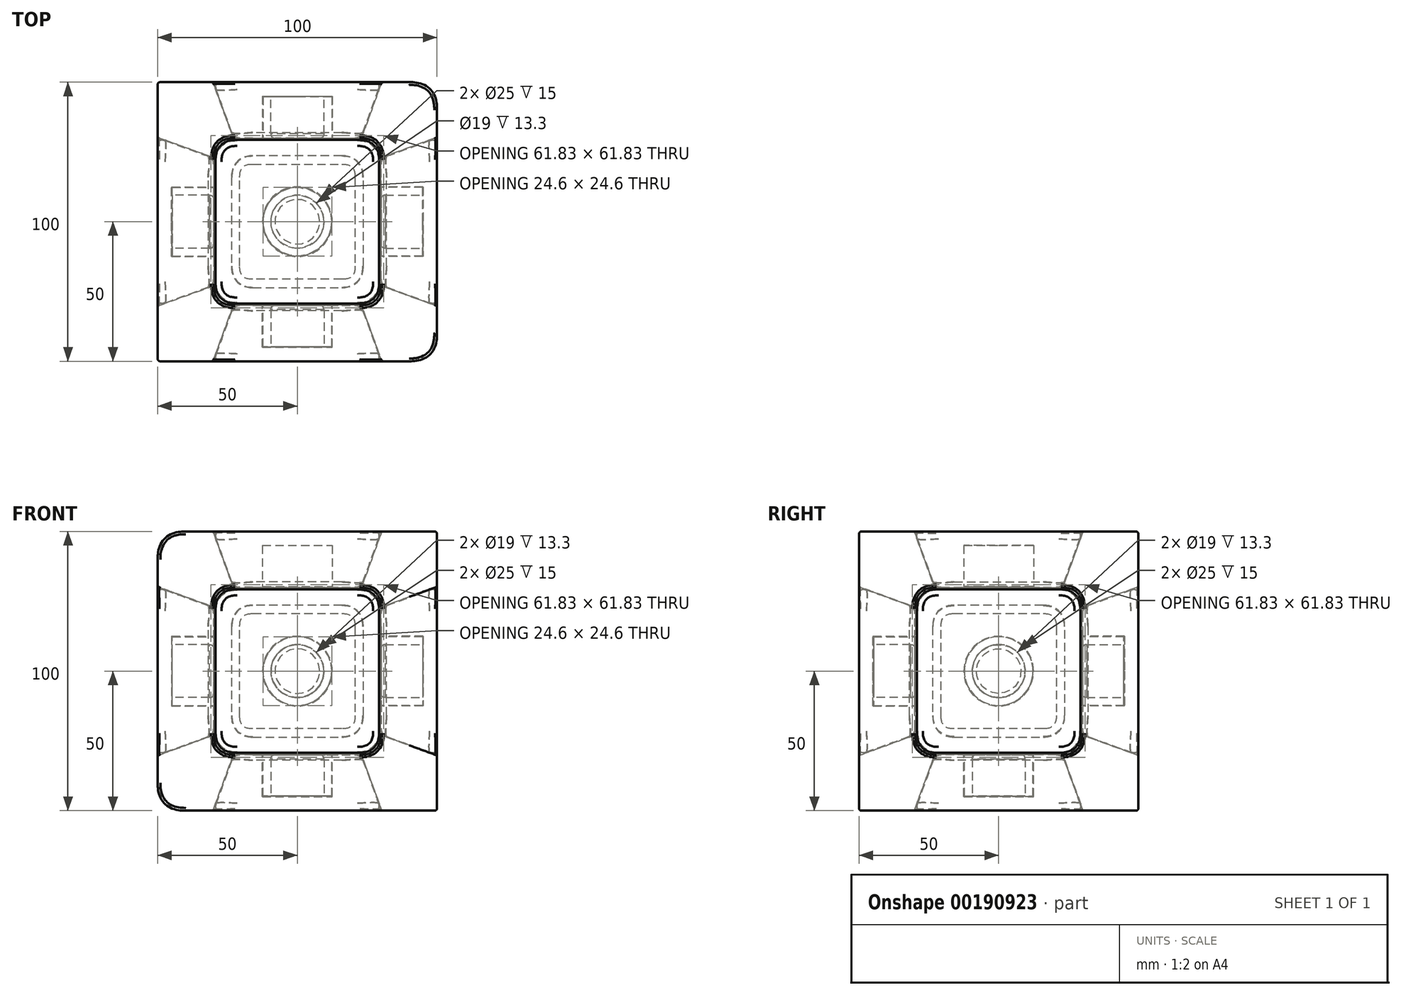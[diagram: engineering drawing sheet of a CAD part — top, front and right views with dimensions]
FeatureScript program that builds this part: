
annotation { "Feature Type Name" : "Feature", "Feature Type Description" : "" }
export const myFeature = defineFeature(function(context is Context, id is Id, definition is map)
    precondition{}
    {
        {
            var Q0;
            Q0=qCreatedBy(makeId("Top.planeOp"),FACE);
            var sketch = newSketch(context, id + "F0", { "sketchPlane" : qUnion([Q0])});
            skLineSegment(sketch, "E0.bottom", {"start": v(50, 50) * mm, "end": v(-50, 50) * mm});
            skLineSegment(sketch, "E0.top", {"start": v(50, -50) * mm, "end": v(-50, -50) * mm});
            skLineSegment(sketch, "E0.left", {"start": v(50, 50) * mm, "end": v(50, -50) * mm});
            skLineSegment(sketch, "E0.right", {"start": v(-50, 50) * mm, "end": v(-50, -50) * mm});
            skPoint(sketch, "E0.middle", {"position": v(0, 0) * mm});
            skSolve(sketch);
        }
        {
            var Q0;
            Q0=qSketchRegion(id+"F0",true);
            extrude(context, id + "F1", {"entities" : qUnion([Q0]), "depth" : 100 * mm, "offsetDistance" : 25 * mm, "symmetric" : true});
        }
        {
            var Q0;
            Q0=makeQuery(id+"F1.opExtrude","CAP_FACE",FACE,{"disambiguationData":[OSD([sQuery(id+"F0.wireOp",EDGE,"E0.bottom"),sQuery(id+"F0.wireOp",EDGE,"E0.top"),sQuery(id+"F0.wireOp",EDGE,"E0.left"),sQuery(id+"F0.wireOp",EDGE,"E0.right")])],"isStart":false});
            var sketch = newSketch(context, id + "F2", { "sketchPlane" : qUnion([Q0])});
            skLineSegment(sketch, "E1.0", {"start": v(30, 30) * mm, "end": v(-30, 30) * mm});
            skLineSegment(sketch, "E1.1", {"start": v(30, 30) * mm, "end": v(30, -30) * mm});
            skLineSegment(sketch, "E1.2", {"start": v(30, -30) * mm, "end": v(-30, -30) * mm});
            skLineSegment(sketch, "E1.3", {"start": v(-30, 30) * mm, "end": v(-30, -30) * mm});
            skSolve(sketch);
        }
        {
            var Q0;
            Q0=qSketchRegion(id+"F2",true);
            extrude(context, id + "F3", {"entities" : qUnion([Q0]), "oppositeDirection" : true, "depth" : 20 * mm, "offsetDistance" : 25 * mm, "hasDraft" : true, "draftAngle" : 20 * degree, "draftPullDirection" : true});
        }
        {
            var Q0;
            Q0=makeQuery(id+"F3.opExtrude","CAP_FACE",FACE,{"disambiguationData":[OSD([sQuery(id+"F2.wireOp",EDGE,"E1.0"),sQuery(id+"F2.wireOp",EDGE,"E1.1"),sQuery(id+"F2.wireOp",EDGE,"E1.2"),sQuery(id+"F2.wireOp",EDGE,"E1.3")])],"isStart":false});
            var sketch = newSketch(context, id + "F4", { "sketchPlane" : qUnion([Q0])});
            skCircle(sketch, "E2", {"center": v(0, 0) * mm, "radius": 12.5 * mm});
            skSolve(sketch);
        }
        {
            var Q0;
            Q0 = qSketchRegion(id + "F4", true);
            extrude(context, id + "F5", {"entities" : qUnion([Q0]), "operationType" : NewBodyOperationType.REMOVE, "oppositeDirection" : true, "depth" : 15 * mm, "offsetDistance" : 25 * mm});
        }
        {
            var Q0;
            Q0=makeQuery(id+"F5.boolean.opBoolean","COPY",FACE,{"derivedFrom":makeQuery(id+"F5.opExtrude","CAP_FACE",FACE,{"disambiguationData":[OSD([sQuery(id+"F4.wireOp",EDGE,"E2")])],"isStart":false})});
            var sketch = newSketch(context, id + "F6", { "sketchPlane" : qUnion([Q0])});
            skCircle(sketch, "E3.0", {"center": v(0, 0) * mm, "radius": 9.5 * mm});
            skSolve(sketch);
        }
        {
            var Q0;
            Q0=makeQuery(id+"F6.imprint","IMPRINT",FACE,{"disambiguationData":[TD([[makeQuery(id+"F6.imprint","IMPRINT",EDGE,{"derivedFrom":sQuery(id+"F6.wireOp",EDGE,"E3.0")}),1.0]])]});
            var Q1;
            Q1=makeQuery(id+"F3.opExtrude","CAP_FACE",FACE,{"disambiguationData":[OSD([sQuery(id+"F2.wireOp",EDGE,"E1.0"),sQuery(id+"F2.wireOp",EDGE,"E1.1"),sQuery(id+"F2.wireOp",EDGE,"E1.2"),sQuery(id+"F2.wireOp",EDGE,"E1.3")])],"isStart":false});
            extrude(context, id + "F7", {"entities" : qUnion([Q0]), "endBound" : BoundingType.UP_TO_SURFACE, "depth" : 25 * mm, "endBoundEntityFace" : qUnion([Q1]), "offsetDistance" : 25 * mm});
        }
        {
            var Q0;
            Q0=qCreatedBy(makeId("Top.planeOp"),FACE);
            var sketch = newSketch(context, id + "F8", { "sketchPlane" : qUnion([Q0])});
            skLineSegment(sketch, "E4", {"start": v(0, -64.23) * mm, "end": v(0, 63.51) * mm, "construction": true});
            skLineSegment(sketch, "E5", {"start": v(-60.37, 0) * mm, "end": v(65.94, 0) * mm, "construction": true});
            skSolve(sketch);
        }
        {
            var Q0;
            Q0=makeQuery(id+"F3.opExtrude","SWEPT_EDGE",EDGE,{"disambiguationData":[OSD([sQuery(id+"F2.wireOp",EDGE,"E1.1"),sQuery(id+"F2.wireOp",EDGE,"E1.2")])]});
            var Q1;
            Q1=makeQuery(id+"F3.opExtrude","SWEPT_EDGE",EDGE,{"disambiguationData":[OSD([sQuery(id+"F2.wireOp",EDGE,"E1.0"),sQuery(id+"F2.wireOp",EDGE,"E1.1")])]});
            var Q2;
            Q2=makeQuery(id+"F3.opExtrude","SWEPT_EDGE",EDGE,{"disambiguationData":[OSD([sQuery(id+"F2.wireOp",EDGE,"E1.2"),sQuery(id+"F2.wireOp",EDGE,"E1.3")])]});
            var Q3;
            Q3=makeQuery(id+"F3.opExtrude","SWEPT_EDGE",EDGE,{"disambiguationData":[OSD([sQuery(id+"F2.wireOp",EDGE,"E1.0"),sQuery(id+"F2.wireOp",EDGE,"E1.3")])]});
            fillet(context, id + "F9", {"entities" : qUnion([Q0, Q1, Q2, Q3]), "tangentPropagation" : true, "crossSection" : FilletCrossSection.CURVATURE, "radius" : 8 * mm, "magnitude" : 0.5, "defaultsChanged" : false, "vertexSettings" : []});
        }
        {
            var Q0;
            Q0=makeQuery(id+"F3.opExtrude","CAP_EDGE",EDGE,{"disambiguationData":[OSD([sQuery(id+"F2.wireOp",EDGE,"E1.1")])],"isStart":false});
            fillet(context, id + "F10", {"entities" : qUnion([Q0]), "tangentPropagation" : true, "crossSection" : FilletCrossSection.CURVATURE, "radius" : 3 * mm, "magnitude" : 0.5, "defaultsChanged" : false, "vertexSettings" : []});
        }
        {
            var Q0;
            Q0=makeQuery(id+"F5.boolean.opBoolean","COPY",EDGE,{"derivedFrom":makeQuery(id+"F5.opExtrude","CAP_EDGE",EDGE,{"disambiguationData":[OSD([sQuery(id+"F4.wireOp",EDGE,"E2")])],"isStart":true})});
            fillet(context, id + "F11", {"entities" : qUnion([Q0]), "tangentPropagation" : true, "crossSection" : FilletCrossSection.CURVATURE, "radius" : 1 * mm, "magnitude" : 0.5, "defaultsChanged" : false, "vertexSettings" : []});
        }
        {
            var Q0;
            Q0=makeQuery(id+"F7.opExtrude","CAP_FACE",FACE,{"disambiguationData":[OSD([sQuery(id+"F6.wireOp",EDGE,"E3.0")])],"isStart":false});
            fillet(context, id + "F12", {"entities" : qUnion([Q0]), "tangentPropagation" : true, "crossSection" : FilletCrossSection.CURVATURE, "radius" : 1.5 * mm, "magnitude" : 0.5, "defaultsChanged" : true, "vertexSettings" : []});
        }
        {
            var Q0;
            Q0=makeQuery(id+"F3.opExtrude","SWEPT_BODY",BODY,{"disambiguationData":[OSD([sQuery(id+"F2.wireOp",EDGE,"E1.0"),sQuery(id+"F2.wireOp",EDGE,"E1.1"),sQuery(id+"F2.wireOp",EDGE,"E1.2"),sQuery(id+"F2.wireOp",EDGE,"E1.3")])]});
            var Q1;
            Q1=makeQuery(id+"F7.opExtrude","SWEPT_BODY",BODY,{"disambiguationData":[OSD([sQuery(id+"F6.wireOp",EDGE,"E3.0")])]});
            var Q2;
            Q2=makeQuery(id+"F3.boolean.opBoolean","COPY",FACE,{"derivedFrom":makeQuery(id+"F3.opExtrude","CAP_FACE",FACE,{"disambiguationData":[OSD([sQuery(id+"F2.wireOp",EDGE,"E1.0"),sQuery(id+"F2.wireOp",EDGE,"E1.1"),sQuery(id+"F2.wireOp",EDGE,"E1.2"),sQuery(id+"F2.wireOp",EDGE,"E1.3")])],"isStart":false})});
            var Q3;
            Q3=makeQuery(id+"F3.boolean.opBoolean","COPY",FACE,{"derivedFrom":makeQuery(id+"F3.opExtrude","SWEPT_FACE",FACE,{"disambiguationData":[OSD([sQuery(id+"F2.wireOp",EDGE,"E1.3")])]})});
            var Q4;
            Q4=makeQuery(id+"F3.boolean.opBoolean","COPY",FACE,{"derivedFrom":makeQuery(id+"F3.opExtrude","SWEPT_FACE",FACE,{"disambiguationData":[OSD([sQuery(id+"F2.wireOp",EDGE,"E1.0")])]})});
            var Q5;
            Q5=makeQuery(id+"F3.boolean.opBoolean","COPY",FACE,{"derivedFrom":makeQuery(id+"F3.opExtrude","SWEPT_FACE",FACE,{"disambiguationData":[OSD([sQuery(id+"F2.wireOp",EDGE,"E1.1")])]})});
            var Q6;
            Q6=makeQuery(id+"F3.boolean.opBoolean","COPY",FACE,{"derivedFrom":makeQuery(id+"F3.opExtrude","SWEPT_FACE",FACE,{"disambiguationData":[OSD([sQuery(id+"F2.wireOp",EDGE,"E1.2")])]})});
            var Q7;
            Q7=sQuery(id+"F8.wireOp",EDGE,"E5");
            circularPattern(context, id + "F13", {"entities" : qUnion([Q0, Q1]), "axis" : qUnion([Q7]), "angle" : 360 * degree, "instanceCount" : 4, "equalSpace" : true});
        }
        {
            var Q0;
            Q0=makeQuery(id+"F3.opExtrude","SWEPT_BODY",BODY,{"disambiguationData":[OSD([sQuery(id+"F2.wireOp",EDGE,"E1.0"),sQuery(id+"F2.wireOp",EDGE,"E1.1"),sQuery(id+"F2.wireOp",EDGE,"E1.2"),sQuery(id+"F2.wireOp",EDGE,"E1.3")])]});
            var Q1;
            Q1=makeQuery(id+"F7.opExtrude","SWEPT_BODY",BODY,{"disambiguationData":[OSD([sQuery(id+"F6.wireOp",EDGE,"E3.0")])]});
            var Q2;
            Q2=makeQuery(id+"F3.boolean.opBoolean","COPY",FACE,{"derivedFrom":makeQuery(id+"F3.opExtrude","CAP_FACE",FACE,{"disambiguationData":[OSD([sQuery(id+"F2.wireOp",EDGE,"E1.0"),sQuery(id+"F2.wireOp",EDGE,"E1.1"),sQuery(id+"F2.wireOp",EDGE,"E1.2"),sQuery(id+"F2.wireOp",EDGE,"E1.3")])],"isStart":false})});
            var Q3;
            Q3=makeQuery(id+"F3.boolean.opBoolean","COPY",FACE,{"derivedFrom":makeQuery(id+"F3.opExtrude","SWEPT_FACE",FACE,{"disambiguationData":[OSD([sQuery(id+"F2.wireOp",EDGE,"E1.3")])]})});
            var Q4;
            Q4=makeQuery(id+"F3.boolean.opBoolean","COPY",FACE,{"derivedFrom":makeQuery(id+"F3.opExtrude","SWEPT_FACE",FACE,{"disambiguationData":[OSD([sQuery(id+"F2.wireOp",EDGE,"E1.0")])]})});
            var Q5;
            Q5=makeQuery(id+"F3.boolean.opBoolean","COPY",FACE,{"derivedFrom":makeQuery(id+"F3.opExtrude","SWEPT_FACE",FACE,{"disambiguationData":[OSD([sQuery(id+"F2.wireOp",EDGE,"E1.1")])]})});
            var Q6;
            Q6=makeQuery(id+"F3.boolean.opBoolean","COPY",FACE,{"derivedFrom":makeQuery(id+"F3.opExtrude","SWEPT_FACE",FACE,{"disambiguationData":[OSD([sQuery(id+"F2.wireOp",EDGE,"E1.2")])]})});
            var Q7;
            Q7=sQuery(id+"F8.wireOp",EDGE,"E4");
            circularPattern(context, id + "F14", {"entities" : qUnion([Q0, Q1]), "axis" : qUnion([Q7]), "angle" : 90 * degree, "instanceCount" : 2, "equalSpace" : true});
        }
        {
            var Q0;
            Q0=makeQuery(id+"F14.opPattern","COPY",BODY,{"derivedFrom":makeQuery(id+"F3.opExtrude","SWEPT_BODY",BODY,{"disambiguationData":[OSD([sQuery(id+"F2.wireOp",EDGE,"E1.0"),sQuery(id+"F2.wireOp",EDGE,"E1.1"),sQuery(id+"F2.wireOp",EDGE,"E1.2"),sQuery(id+"F2.wireOp",EDGE,"E1.3")])]}),"instanceName":"1"});
            var Q1;
            Q1=makeQuery(id+"F14.opPattern","COPY",BODY,{"derivedFrom":makeQuery(id+"F7.opExtrude","SWEPT_BODY",BODY,{"disambiguationData":[OSD([sQuery(id+"F6.wireOp",EDGE,"E3.0")])]}),"instanceName":"1"});
            var Q2;
            Q2=makeQuery(id+"F14.opPattern","COPY",FACE,{"derivedFrom":makeQuery(id+"F3.boolean.opBoolean","COPY",FACE,{"derivedFrom":makeQuery(id+"F3.opExtrude","CAP_FACE",FACE,{"disambiguationData":[OSD([sQuery(id+"F2.wireOp",EDGE,"E1.0"),sQuery(id+"F2.wireOp",EDGE,"E1.1"),sQuery(id+"F2.wireOp",EDGE,"E1.2"),sQuery(id+"F2.wireOp",EDGE,"E1.3")])],"isStart":false})}),"instanceName":"1"});
            var Q3;
            Q3=makeQuery(id+"F14.opPattern","COPY",FACE,{"derivedFrom":makeQuery(id+"F3.boolean.opBoolean","COPY",FACE,{"derivedFrom":makeQuery(id+"F3.opExtrude","SWEPT_FACE",FACE,{"disambiguationData":[OSD([sQuery(id+"F2.wireOp",EDGE,"E1.3")])]})}),"instanceName":"1"});
            var Q4;
            Q4=makeQuery(id+"F14.opPattern","COPY",FACE,{"derivedFrom":makeQuery(id+"F3.boolean.opBoolean","COPY",FACE,{"derivedFrom":makeQuery(id+"F3.opExtrude","SWEPT_FACE",FACE,{"disambiguationData":[OSD([sQuery(id+"F2.wireOp",EDGE,"E1.0")])]})}),"instanceName":"1"});
            var Q5;
            Q5=makeQuery(id+"F14.opPattern","COPY",FACE,{"derivedFrom":makeQuery(id+"F3.boolean.opBoolean","COPY",FACE,{"derivedFrom":makeQuery(id+"F3.opExtrude","SWEPT_FACE",FACE,{"disambiguationData":[OSD([sQuery(id+"F2.wireOp",EDGE,"E1.2")])]})}),"instanceName":"1"});
            var Q6;
            Q6=makeQuery(id+"F14.opPattern","COPY",FACE,{"derivedFrom":makeQuery(id+"F3.boolean.opBoolean","COPY",FACE,{"derivedFrom":makeQuery(id+"F3.opExtrude","SWEPT_FACE",FACE,{"disambiguationData":[OSD([sQuery(id+"F2.wireOp",EDGE,"E1.1")])]})}),"instanceName":"1"});
            var Q7;
            Q7=qCreatedBy(makeId("Right.planeOp"),FACE);
            mirror(context, id + "F15", {"entities" : qUnion([Q0, Q1]), "faces" : qUnion([Q2, Q3, Q4, Q5, Q6]), "mirrorPlane" : qUnion([Q7])});
        }
        {
            var Q0;
            Q0=makeQuery(id+"F3.opExtrude","SWEPT_BODY",BODY,{"disambiguationData":[OSD([sQuery(id+"F2.wireOp",EDGE,"E1.0"),sQuery(id+"F2.wireOp",EDGE,"E1.1"),sQuery(id+"F2.wireOp",EDGE,"E1.2"),sQuery(id+"F2.wireOp",EDGE,"E1.3")])]});
            var Q1;
            Q1=makeQuery(id+"F13.opPattern","COPY",BODY,{"derivedFrom":makeQuery(id+"F3.opExtrude","SWEPT_BODY",BODY,{"disambiguationData":[OSD([sQuery(id+"F2.wireOp",EDGE,"E1.0"),sQuery(id+"F2.wireOp",EDGE,"E1.1"),sQuery(id+"F2.wireOp",EDGE,"E1.2"),sQuery(id+"F2.wireOp",EDGE,"E1.3")])]}),"instanceName":"1"});
            var Q2;
            Q2=makeQuery(id+"F13.opPattern","COPY",BODY,{"derivedFrom":makeQuery(id+"F3.opExtrude","SWEPT_BODY",BODY,{"disambiguationData":[OSD([sQuery(id+"F2.wireOp",EDGE,"E1.0"),sQuery(id+"F2.wireOp",EDGE,"E1.1"),sQuery(id+"F2.wireOp",EDGE,"E1.2"),sQuery(id+"F2.wireOp",EDGE,"E1.3")])]}),"instanceName":"2"});
            var Q3;
            Q3=makeQuery(id+"F13.opPattern","COPY",BODY,{"derivedFrom":makeQuery(id+"F3.opExtrude","SWEPT_BODY",BODY,{"disambiguationData":[OSD([sQuery(id+"F2.wireOp",EDGE,"E1.0"),sQuery(id+"F2.wireOp",EDGE,"E1.1"),sQuery(id+"F2.wireOp",EDGE,"E1.2"),sQuery(id+"F2.wireOp",EDGE,"E1.3")])]}),"instanceName":"3"});
            var Q4;
            Q4=makeQuery(id+"F15.opPattern","COPY",BODY,{"derivedFrom":makeQuery(id+"F14.opPattern","COPY",BODY,{"derivedFrom":makeQuery(id+"F3.opExtrude","SWEPT_BODY",BODY,{"disambiguationData":[OSD([sQuery(id+"F2.wireOp",EDGE,"E1.0"),sQuery(id+"F2.wireOp",EDGE,"E1.1"),sQuery(id+"F2.wireOp",EDGE,"E1.2"),sQuery(id+"F2.wireOp",EDGE,"E1.3")])]}),"instanceName":"1"}),"instanceName":"1"});
            var Q5;
            Q5=makeQuery(id+"F14.opPattern","COPY",BODY,{"derivedFrom":makeQuery(id+"F3.opExtrude","SWEPT_BODY",BODY,{"disambiguationData":[OSD([sQuery(id+"F2.wireOp",EDGE,"E1.0"),sQuery(id+"F2.wireOp",EDGE,"E1.1"),sQuery(id+"F2.wireOp",EDGE,"E1.2"),sQuery(id+"F2.wireOp",EDGE,"E1.3")])]}),"instanceName":"1"});
            var Q6;
            Q6=makeQuery(id+"F1.opExtrude","SWEPT_BODY",BODY,{"disambiguationData":[OSD([sQuery(id+"F0.wireOp",EDGE,"E0.bottom"),sQuery(id+"F0.wireOp",EDGE,"E0.top"),sQuery(id+"F0.wireOp",EDGE,"E0.left"),sQuery(id+"F0.wireOp",EDGE,"E0.right")])]});
            booleanBodies(context, id + "F16", {"operationType" : BooleanOperationType.SUBTRACTION, "tools" : qUnion([Q0, Q1, Q2, Q3, Q4, Q5]), "targets" : qUnion([Q6]), "offset" : true, "offsetAll" : true, "offsetDistance" : 0.2 * mm, "keepTools" : true});
        }
        {
            var Q0;
            Q0=makeQuery(id+"F7.opExtrude","SWEPT_BODY",BODY,{"disambiguationData":[OSD([sQuery(id+"F6.wireOp",EDGE,"E3.0")])]});
            var Q1;
            Q1=makeQuery(id+"F15.opPattern","COPY",BODY,{"derivedFrom":makeQuery(id+"F14.opPattern","COPY",BODY,{"derivedFrom":makeQuery(id+"F7.opExtrude","SWEPT_BODY",BODY,{"disambiguationData":[OSD([sQuery(id+"F6.wireOp",EDGE,"E3.0")])]}),"instanceName":"1"}),"instanceName":"1"});
            var Q2;
            Q2=makeQuery(id+"F13.opPattern","COPY",BODY,{"derivedFrom":makeQuery(id+"F7.opExtrude","SWEPT_BODY",BODY,{"disambiguationData":[OSD([sQuery(id+"F6.wireOp",EDGE,"E3.0")])]}),"instanceName":"2"});
            var Q3;
            Q3=makeQuery(id+"F14.opPattern","COPY",BODY,{"derivedFrom":makeQuery(id+"F7.opExtrude","SWEPT_BODY",BODY,{"disambiguationData":[OSD([sQuery(id+"F6.wireOp",EDGE,"E3.0")])]}),"instanceName":"1"});
            var Q4;
            Q4=makeQuery(id+"F13.opPattern","COPY",BODY,{"derivedFrom":makeQuery(id+"F7.opExtrude","SWEPT_BODY",BODY,{"disambiguationData":[OSD([sQuery(id+"F6.wireOp",EDGE,"E3.0")])]}),"instanceName":"3"});
            var Q5;
            Q5=makeQuery(id+"F13.opPattern","COPY",BODY,{"derivedFrom":makeQuery(id+"F7.opExtrude","SWEPT_BODY",BODY,{"disambiguationData":[OSD([sQuery(id+"F6.wireOp",EDGE,"E3.0")])]}),"instanceName":"1"});
            var Q6;
            Q6=makeQuery(id+"F1.opExtrude","SWEPT_BODY",BODY,{"disambiguationData":[OSD([sQuery(id+"F0.wireOp",EDGE,"E0.bottom"),sQuery(id+"F0.wireOp",EDGE,"E0.top"),sQuery(id+"F0.wireOp",EDGE,"E0.left"),sQuery(id+"F0.wireOp",EDGE,"E0.right")])]});
            booleanBodies(context, id + "F17", {"operationType" : BooleanOperationType.SUBTRACTION, "tools" : qUnion([Q0, Q1, Q2, Q3, Q4, Q5]), "targets" : qUnion([Q6])});
        }
        {
            var Q0;
            Q0=makeQuery(id+"F1.opExtrude","SWEPT_EDGE",EDGE,{"disambiguationData":[OSD([sQuery(id+"F0.wireOp",EDGE,"E0.top"),sQuery(id+"F0.wireOp",EDGE,"E0.left")])]});
            var Q1;
            Q1=makeQuery(id+"F1.opExtrude","CAP_EDGE",EDGE,{"disambiguationData":[OSD([sQuery(id+"F0.wireOp",EDGE,"E0.right")])],"isStart":false});
            var Q2;
            Q2=makeQuery(id+"F1.opExtrude","CAP_EDGE",EDGE,{"disambiguationData":[OSD([sQuery(id+"F0.wireOp",EDGE,"E0.right")])],"isStart":true});
            var Q3;
            Q3=makeQuery(id+"F1.opExtrude","SWEPT_EDGE",EDGE,{"disambiguationData":[OSD([sQuery(id+"F0.wireOp",EDGE,"E0.bottom"),sQuery(id+"F0.wireOp",EDGE,"E0.left")])]});
            fillet(context, id + "F18", {"entities" : qUnion([Q0, Q1, Q2, Q3]), "tangentPropagation" : true, "crossSection" : FilletCrossSection.CURVATURE, "radius" : 10 * mm, "magnitude" : 0.5, "defaultsChanged" : true, "vertexSettings" : []});
        }
        {
            var Q0;
            Q0=makeQuery(id+"F1.opExtrude","SWEPT_EDGE",EDGE,{"disambiguationData":[OSD([sQuery(id+"F0.wireOp",EDGE,"E0.top"),sQuery(id+"F0.wireOp",EDGE,"E0.right")])]});
            fillet(context, id + "F19", {"entities" : qUnion([Q0]), "tangentPropagation" : true, "crossSection" : FilletCrossSection.CURVATURE, "radius" : 1 * mm, "magnitude" : 0.5, "defaultsChanged" : false, "vertexSettings" : []});
        }
        {
            var Q0;
            Q0=makeQuery(id+"F16.tempBoolean.opBoolean","INTERSECT",EDGE,{"derivedFrom":[makeQuery(id+"F1.opExtrude","CAP_FACE",FACE,{"disambiguationData":[OSD([sQuery(id+"F0.wireOp",EDGE,"E0.bottom"),sQuery(id+"F0.wireOp",EDGE,"E0.top"),sQuery(id+"F0.wireOp",EDGE,"E0.left"),sQuery(id+"F0.wireOp",EDGE,"E0.right")])],"isStart":false}),makeQuery(id+"F16.offsetTempBody.opPattern","COPY",FACE,{"derivedFrom":makeQuery(id+"F3.opExtrude","SWEPT_FACE",FACE,{"disambiguationData":[OSD([sQuery(id+"F2.wireOp",EDGE,"E1.3")])]}),"instanceName":"1"})]});
            var Q1;
            Q1=makeQuery(id+"F16.tempBoolean.opBoolean","INTERSECT",EDGE,{"derivedFrom":[makeQuery(id+"F1.opExtrude","SWEPT_FACE",FACE,{"disambiguationData":[OSD([sQuery(id+"F0.wireOp",EDGE,"E0.right")])]}),makeQuery(id+"F16.offsetTempBody.opPattern","COPY",FACE,{"derivedFrom":makeQuery(id+"F15.opPattern","COPY",FACE,{"derivedFrom":makeQuery(id+"F14.opPattern","COPY",FACE,{"derivedFrom":makeQuery(id+"F3.opExtrude","SWEPT_FACE",FACE,{"disambiguationData":[OSD([sQuery(id+"F2.wireOp",EDGE,"E1.1")])]}),"instanceName":"1"}),"instanceName":"1"}),"instanceName":"1"})]});
            var Q2;
            Q2=makeQuery(id+"F16.tempBoolean.opBoolean","INTERSECT",EDGE,{"derivedFrom":[makeQuery(id+"F1.opExtrude","CAP_FACE",FACE,{"disambiguationData":[OSD([sQuery(id+"F0.wireOp",EDGE,"E0.bottom"),sQuery(id+"F0.wireOp",EDGE,"E0.top"),sQuery(id+"F0.wireOp",EDGE,"E0.left"),sQuery(id+"F0.wireOp",EDGE,"E0.right")])],"isStart":true}),makeQuery(id+"F16.offsetTempBody.opPattern","COPY",FACE,{"derivedFrom":makeQuery(id+"F13.opPattern","COPY",FACE,{"derivedFrom":makeQuery(id+"F3.opExtrude","SWEPT_FACE",FACE,{"disambiguationData":[OSD([sQuery(id+"F2.wireOp",EDGE,"E1.1")])]}),"instanceName":"2"}),"instanceName":"1"})]});
            var Q3;
            Q3=makeQuery(id+"F16.tempBoolean.opBoolean","INTERSECT",EDGE,{"derivedFrom":[makeQuery(id+"F1.opExtrude","SWEPT_FACE",FACE,{"disambiguationData":[OSD([sQuery(id+"F0.wireOp",EDGE,"E0.left")])]}),makeQuery(id+"F16.offsetTempBody.opPattern","COPY",FACE,{"derivedFrom":makeQuery(id+"F14.opPattern","COPY",FACE,{"derivedFrom":makeQuery(id+"F3.opExtrude","SWEPT_FACE",FACE,{"disambiguationData":[OSD([sQuery(id+"F2.wireOp",EDGE,"E1.1")])]}),"instanceName":"1"}),"instanceName":"1"})]});
            var Q4;
            Q4=makeQuery(id+"F16.tempBoolean.opBoolean","INTERSECT",EDGE,{"derivedFrom":[makeQuery(id+"F1.opExtrude","SWEPT_FACE",FACE,{"disambiguationData":[OSD([sQuery(id+"F0.wireOp",EDGE,"E0.bottom")])]}),makeQuery(id+"F16.offsetTempBody.opPattern","COPY",FACE,{"derivedFrom":makeQuery(id+"F13.opPattern","COPY",FACE,{"derivedFrom":makeQuery(id+"F3.opExtrude","SWEPT_FACE",FACE,{"disambiguationData":[OSD([sQuery(id+"F2.wireOp",EDGE,"E1.2")])]}),"instanceName":"3"}),"instanceName":"1"})]});
            var Q5;
            Q5=makeQuery(id+"F16.tempBoolean.opBoolean","INTERSECT",EDGE,{"derivedFrom":[makeQuery(id+"F1.opExtrude","SWEPT_FACE",FACE,{"disambiguationData":[OSD([sQuery(id+"F0.wireOp",EDGE,"E0.top")])]}),makeQuery(id+"F16.offsetTempBody.opPattern","COPY",FACE,{"derivedFrom":makeQuery(id+"F13.opPattern","COPY",FACE,{"derivedFrom":makeQuery(id+"F3.opExtrude","SWEPT_FACE",FACE,{"disambiguationData":[OSD([sQuery(id+"F2.wireOp",EDGE,"E1.0")])]}),"instanceName":"1"}),"instanceName":"1"})]});
            fillet(context, id + "F20", {"entities" : qUnion([Q0, Q1, Q2, Q3, Q4, Q5]), "tangentPropagation" : true, "crossSection" : FilletCrossSection.CURVATURE, "radius" : 1 * mm, "magnitude" : 0.5, "defaultsChanged" : false, "vertexSettings" : []});
        }
        {
            var Q0;
            Q0=makeQuery(id+"F3.opExtrude","CAP_FACE",FACE,{"disambiguationData":[OSD([sQuery(id+"F2.wireOp",EDGE,"E1.0"),sQuery(id+"F2.wireOp",EDGE,"E1.1"),sQuery(id+"F2.wireOp",EDGE,"E1.2"),sQuery(id+"F2.wireOp",EDGE,"E1.3")])],"isStart":true});
            var Q1;
            Q1=makeQuery(id+"F13.opPattern","COPY",FACE,{"derivedFrom":makeQuery(id+"F3.opExtrude","CAP_FACE",FACE,{"disambiguationData":[OSD([sQuery(id+"F2.wireOp",EDGE,"E1.0"),sQuery(id+"F2.wireOp",EDGE,"E1.1"),sQuery(id+"F2.wireOp",EDGE,"E1.2"),sQuery(id+"F2.wireOp",EDGE,"E1.3")])],"isStart":true}),"instanceName":"1"});
            var Q2;
            Q2=makeQuery(id+"F13.opPattern","COPY",FACE,{"derivedFrom":makeQuery(id+"F3.opExtrude","CAP_FACE",FACE,{"disambiguationData":[OSD([sQuery(id+"F2.wireOp",EDGE,"E1.0"),sQuery(id+"F2.wireOp",EDGE,"E1.1"),sQuery(id+"F2.wireOp",EDGE,"E1.2"),sQuery(id+"F2.wireOp",EDGE,"E1.3")])],"isStart":true}),"instanceName":"2"});
            var Q3;
            Q3=makeQuery(id+"F13.opPattern","COPY",FACE,{"derivedFrom":makeQuery(id+"F3.opExtrude","CAP_FACE",FACE,{"disambiguationData":[OSD([sQuery(id+"F2.wireOp",EDGE,"E1.0"),sQuery(id+"F2.wireOp",EDGE,"E1.1"),sQuery(id+"F2.wireOp",EDGE,"E1.2"),sQuery(id+"F2.wireOp",EDGE,"E1.3")])],"isStart":true}),"instanceName":"3"});
            var Q4;
            Q4=makeQuery(id+"F14.opPattern","COPY",FACE,{"derivedFrom":makeQuery(id+"F3.opExtrude","CAP_FACE",FACE,{"disambiguationData":[OSD([sQuery(id+"F2.wireOp",EDGE,"E1.0"),sQuery(id+"F2.wireOp",EDGE,"E1.1"),sQuery(id+"F2.wireOp",EDGE,"E1.2"),sQuery(id+"F2.wireOp",EDGE,"E1.3")])],"isStart":true}),"instanceName":"1"});
            var Q5;
            Q5=makeQuery(id+"F15.opPattern","COPY",FACE,{"derivedFrom":makeQuery(id+"F14.opPattern","COPY",FACE,{"derivedFrom":makeQuery(id+"F3.opExtrude","CAP_FACE",FACE,{"disambiguationData":[OSD([sQuery(id+"F2.wireOp",EDGE,"E1.0"),sQuery(id+"F2.wireOp",EDGE,"E1.1"),sQuery(id+"F2.wireOp",EDGE,"E1.2"),sQuery(id+"F2.wireOp",EDGE,"E1.3")])],"isStart":true}),"instanceName":"1"}),"instanceName":"1"});
            fillet(context, id + "F21", {"entities" : qUnion([Q0, Q1, Q2, Q3, Q4, Q5]), "tangentPropagation" : true, "crossSection" : FilletCrossSection.CURVATURE, "radius" : 2 * mm, "magnitude" : 0.5, "defaultsChanged" : true, "vertexSettings" : []});
        }
    });
